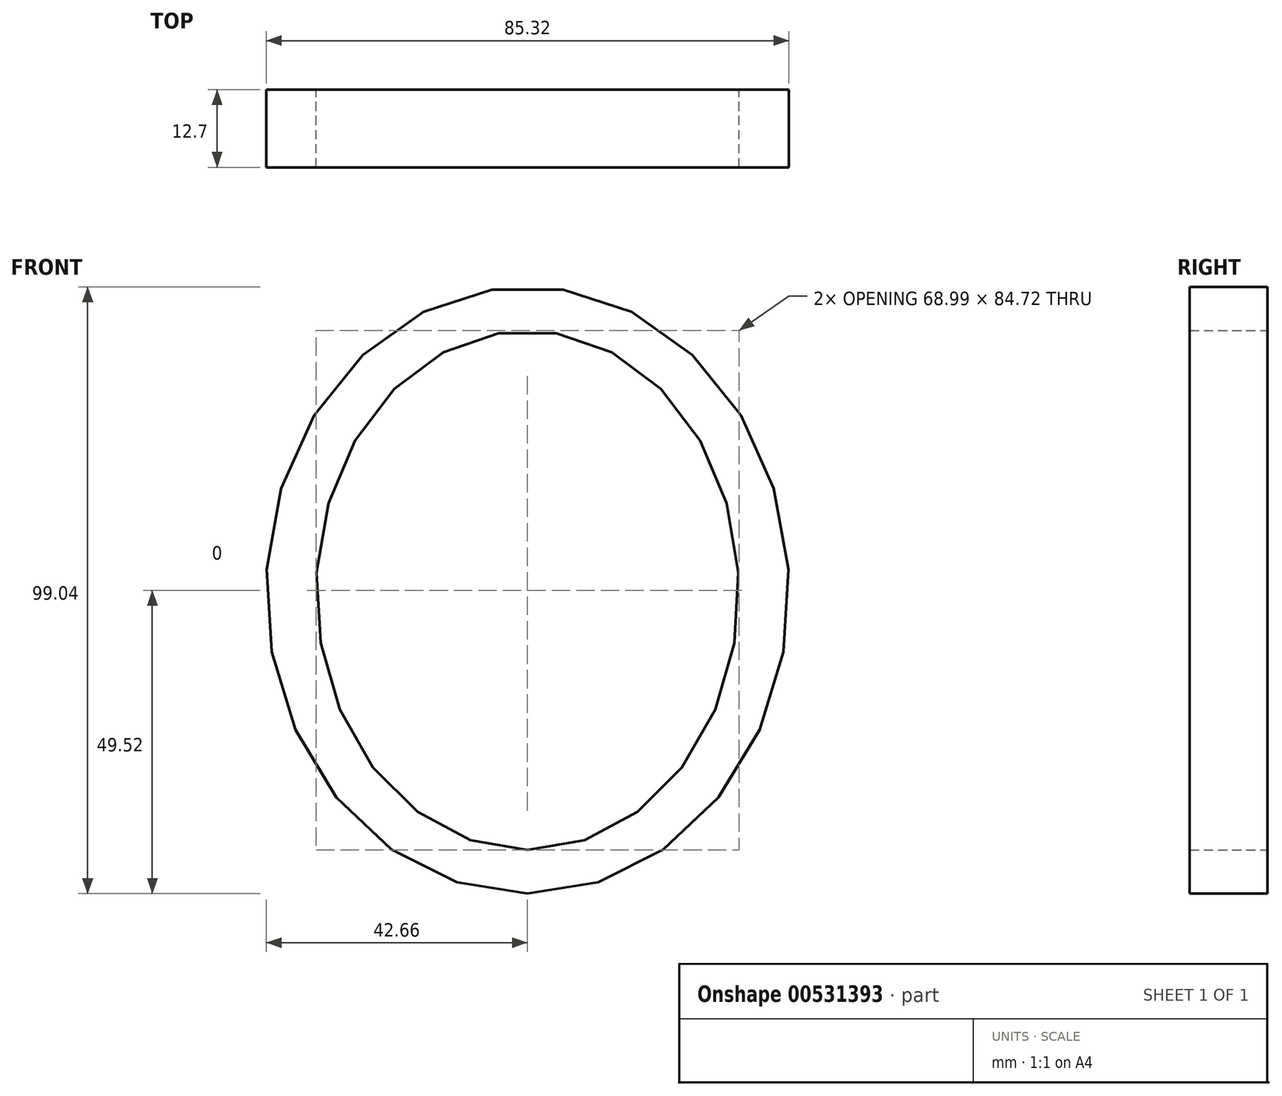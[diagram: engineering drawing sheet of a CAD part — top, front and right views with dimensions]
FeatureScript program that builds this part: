
annotation { "Feature Type Name" : "Feature", "Feature Type Description" : "" }
export const myFeature = defineFeature(function(context is Context, id is Id, definition is map)
    precondition{}
    {
        {
            var Q0;
            Q0=qCreatedBy(makeId("Front.planeOp"),FACE);
            var sketch = newSketch(context, id + "F0", { "sketchPlane" : qUnion([Q0])});
            skEllipse(sketch, "E0", {"center": v(0, 0) * mm, "majorRadius": 49.52 * mm, "minorRadius": 42.66 * mm, "majorAxis": v(0, -1)});
            skEllipse(sketch, "E1", {"center": v(0, 0) * mm, "majorRadius": 42.36 * mm, "minorRadius": 34.5 * mm, "majorAxis": v(0, -1)});
            skSolve(sketch);
        }
        {
            var Q0;
            Q0=makeQuery(id+"F0.imprint","IMPRINT",FACE,{"disambiguationData":[TD([[makeQuery(id+"F0.imprint","IMPRINT",EDGE,{"derivedFrom":sQuery(id+"F0.wireOp",EDGE,"E0")}),1.0]])]});
            extrude(context, id + "F1", {"entities" : qUnion([Q0]), "endBound" : BoundingType.SYMMETRIC, "depth" : 12.7 * mm, "offsetDistance" : 25.4 * mm});
        }
    });
